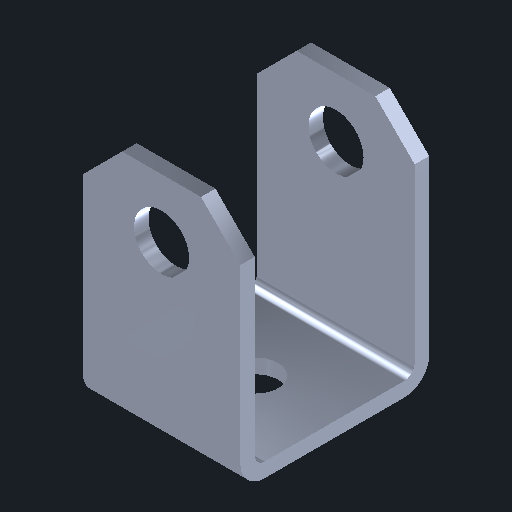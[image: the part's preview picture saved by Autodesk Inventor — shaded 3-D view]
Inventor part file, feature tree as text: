
AUTODESK INVENTOR PART (.ipt)
format: ipt  version: 2024 (Build 280153000, 153)  size: 157,696 bytes
history: native  units: in
note: dims shown in document units (in); Inventor stores cm internally (conversion verified against a paired STEP export)
features: chamfer x1, other x1, imported_body x1
ambient origin geometry x8: Origin, YZ Plane, XZ Plane, XY Plane, X Axis, Y Axis, Z Axis, Center Point
bodies: Body1 (feature_tree)
feature tree (3):
  chamfer  "Chamfer1"  [1 undecoded]
  other  "VL-PNEU-BRK-0011"
  imported_body  "Base1"
note: 1 required parameter value undecoded (feature->parameter linkage not recoverable at this tier; creation-order binding heuristic only, values carry confidence <= 0.55)
